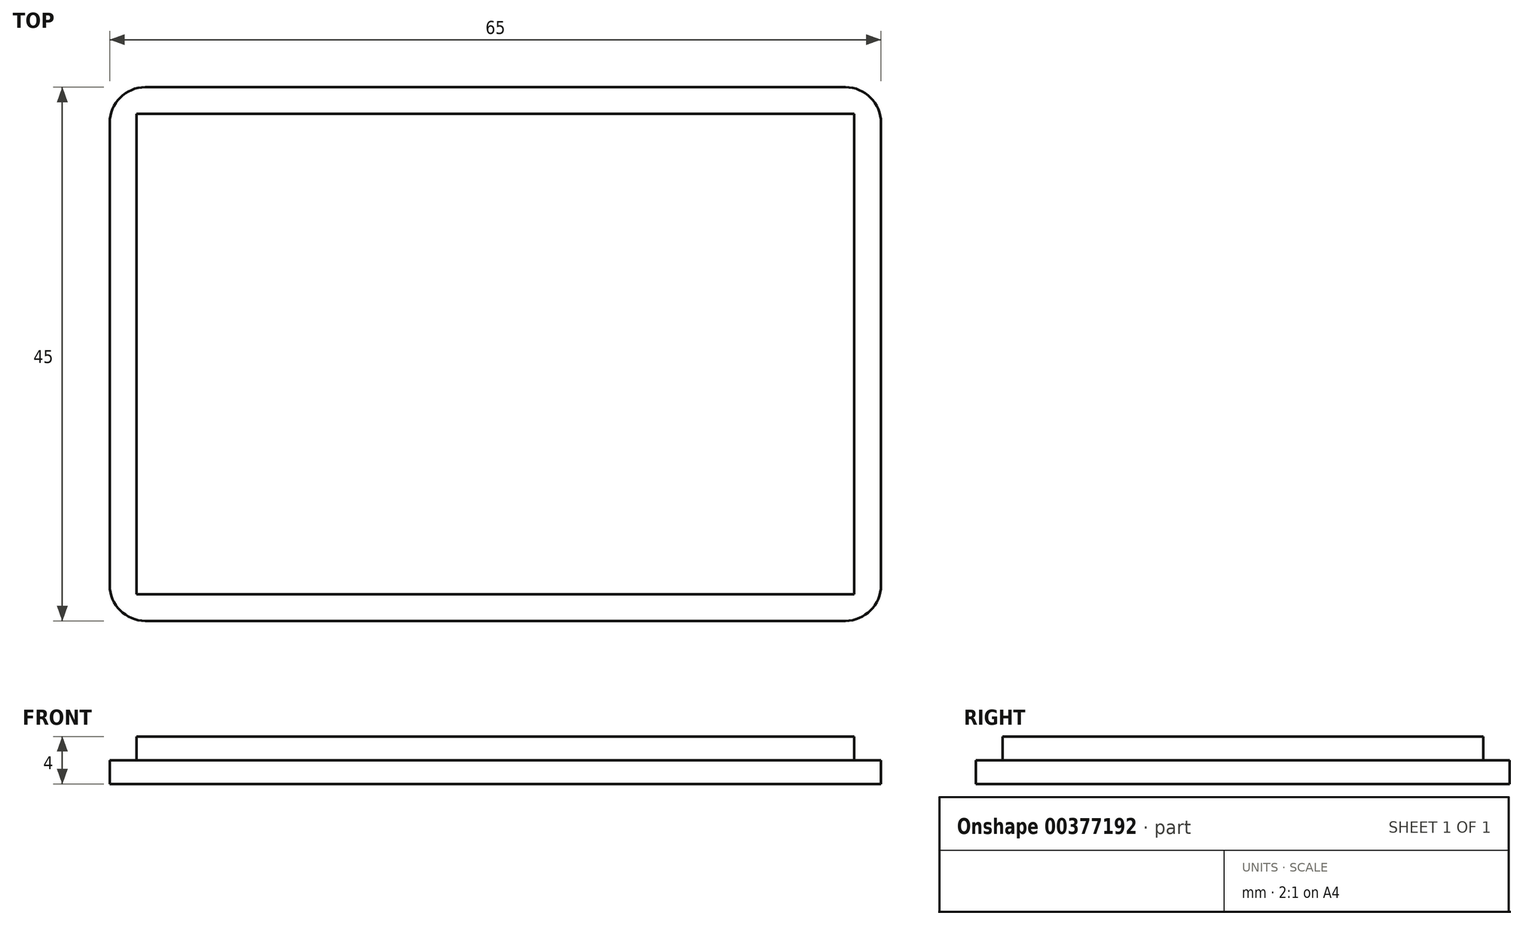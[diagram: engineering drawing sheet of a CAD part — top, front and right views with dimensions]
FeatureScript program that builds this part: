
annotation { "Feature Type Name" : "Feature", "Feature Type Description" : "" }
export const myFeature = defineFeature(function(context is Context, id is Id, definition is map)
    precondition{}
    {
        {
            var Q0;
            Q0=qCreatedBy(makeId("Top.planeOp"),FACE);
            var sketch = newSketch(context, id + "F0", { "sketchPlane" : qUnion([Q0])});
            skLineSegment(sketch, "E0.bottom", {"start": v(32.5, 22.5) * mm, "end": v(-32.5, 22.5) * mm});
            skLineSegment(sketch, "E0.top", {"start": v(32.5, -22.5) * mm, "end": v(-32.5, -22.5) * mm});
            skLineSegment(sketch, "E0.left", {"start": v(32.5, 22.5) * mm, "end": v(32.5, -22.5) * mm});
            skLineSegment(sketch, "E0.right", {"start": v(-32.5, 22.5) * mm, "end": v(-32.5, -22.5) * mm});
            skPoint(sketch, "E0.middle", {"position": v(0, 0) * mm});
            skLineSegment(sketch, "E1.bottom", {"start": v(30.25, -20.25) * mm, "end": v(-30.25, -20.25) * mm});
            skLineSegment(sketch, "E1.top", {"start": v(30.25, 20.25) * mm, "end": v(-30.25, 20.25) * mm});
            skLineSegment(sketch, "E1.left", {"start": v(30.25, -20.25) * mm, "end": v(30.25, 20.25) * mm});
            skLineSegment(sketch, "E1.right", {"start": v(-30.25, -20.25) * mm, "end": v(-30.25, 20.25) * mm});
            skLineSegment(sketch, "E2.bottom", {"start": v(26, -16) * mm, "end": v(-26, -16) * mm});
            skLineSegment(sketch, "E2.top", {"start": v(26, 16) * mm, "end": v(-26, 16) * mm});
            skLineSegment(sketch, "E2.left", {"start": v(26, -16) * mm, "end": v(26, 16) * mm});
            skLineSegment(sketch, "E2.right", {"start": v(-26, -16) * mm, "end": v(-26, 16) * mm});
            skSolve(sketch);
        }
        {
            var Q0;
            Q0=makeQuery(id+"F0.imprint","IMPRINT",FACE,{"disambiguationData":[TD([[makeQuery(id+"F0.imprint","IMPRINT",EDGE,{"derivedFrom":sQuery(id+"F0.wireOp",EDGE,"E0.bottom")}),1.0]])]});
            extrude(context, id + "F1", {"entities" : qUnion([Q0]), "depth" : 2 * mm});
        }
        {
            var Q0;
            Q0=makeQuery(id+"F0.imprint","IMPRINT",FACE,{"disambiguationData":[TD([[makeQuery(id+"F0.imprint","IMPRINT",EDGE,{"derivedFrom":sQuery(id+"F0.wireOp",EDGE,"E1.bottom")}),-1.0]])]});
            var Q1;
            Q1=makeQuery(id+"F0.imprint","IMPRINT",FACE,{"disambiguationData":[TD([[makeQuery(id+"F0.imprint","IMPRINT",EDGE,{"derivedFrom":sQuery(id+"F0.wireOp",EDGE,"E2.bottom")}),-1.0]])]});
            extrude(context, id + "F2", {"entities" : qUnion([Q0, Q1]), "operationType" : NewBodyOperationType.ADD, "depth" : 4 * mm});
        }
        {
            var Q0;
            Q0=makeQuery(id+"F1.opExtrude","SWEPT_EDGE",EDGE,{"disambiguationData":[OSD([sQuery(id+"F0.wireOp",EDGE,"E0.bottom"),sQuery(id+"F0.wireOp",EDGE,"E0.right")])]});
            var Q1;
            Q1=makeQuery(id+"F1.opExtrude","SWEPT_EDGE",EDGE,{"disambiguationData":[OSD([sQuery(id+"F0.wireOp",EDGE,"E0.bottom"),sQuery(id+"F0.wireOp",EDGE,"E0.left")])]});
            var Q2;
            Q2=makeQuery(id+"F1.opExtrude","SWEPT_EDGE",EDGE,{"disambiguationData":[OSD([sQuery(id+"F0.wireOp",EDGE,"E0.top"),sQuery(id+"F0.wireOp",EDGE,"E0.left")])]});
            var Q3;
            Q3=makeQuery(id+"F1.opExtrude","SWEPT_EDGE",EDGE,{"disambiguationData":[OSD([sQuery(id+"F0.wireOp",EDGE,"E0.top"),sQuery(id+"F0.wireOp",EDGE,"E0.right")])]});
            fillet(context, id + "F3", {"entities" : qUnion([Q0, Q1, Q2, Q3]), "radius" : 3 * mm, "tangentPropagation" : true, "allowEdgeOverflow" : false});
        }
    });
